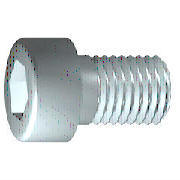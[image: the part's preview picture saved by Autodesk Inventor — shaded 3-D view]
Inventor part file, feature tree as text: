
AUTODESK INVENTOR PART (.ipt)
format: ipt  version: 2014 (Build 180170000, 170)  size: 197,120 bytes
history: native  units: mm (DEFAULTED — no unit token found)
features: sketch x2, extrude x1, plane x1, fillet x1
ambient origin geometry x7: Origin, YZ Plane, XY Plane, X Axis, Y Axis, Z Axis, Center Point
bodies: Solid1 (feature_tree), Body (feature_tree)
feature tree (5):
  extrude  "Slot"  Depth=2.8448mm
  plane  "Work Plane1"
  fillet  "Fillet2"  Radius=2.8448mm
  sketch  "Sketch1"  dims[d1=5.49275mm d2=1.5876mm d3=2.8448mm]
  sketch  "Sketch2"  dims[d4=1.2954mm d5=60.0deg d6=2.8448mm d7=2.8448mm d8=2.756963mm d9=4.6482mm d10=90.0deg d11=10.0mm d12=0.0mm d13=5.49275mm d14=0.0mm d15=0.37846mm d16=0.37846mm d17=0.2286mm d19=0.0mm d26=7.9375mm d27=45.0deg d28=0.0mm d29=0.0mm d30=0.1016mm]
